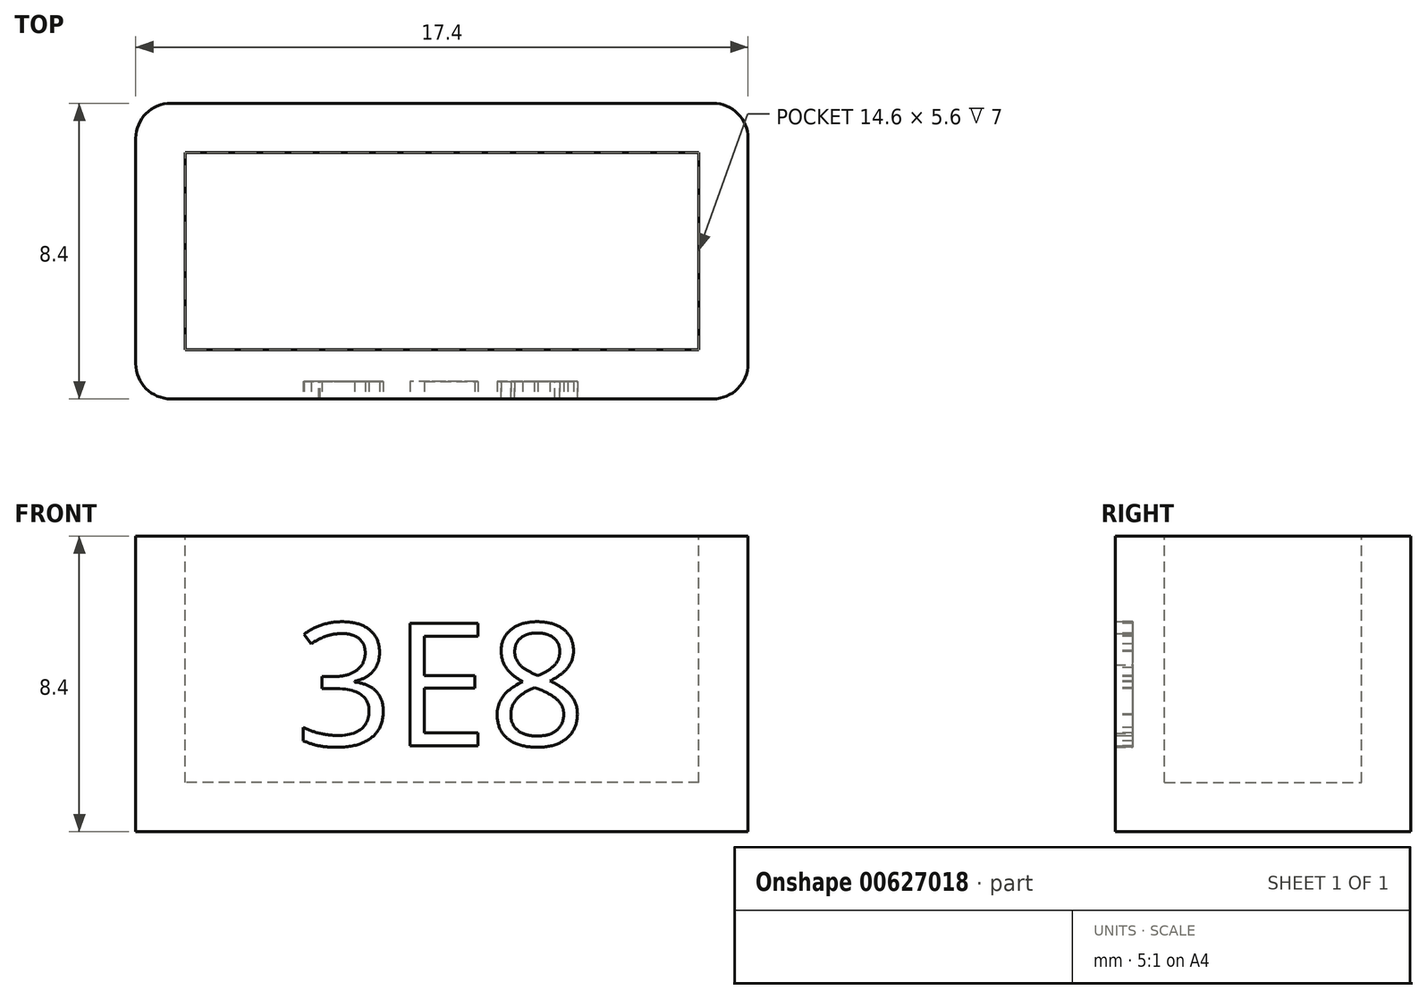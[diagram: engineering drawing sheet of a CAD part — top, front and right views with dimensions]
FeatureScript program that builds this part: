
annotation { "Feature Type Name" : "Feature", "Feature Type Description" : "" }
export const myFeature = defineFeature(function(context is Context, id is Id, definition is map)
    precondition{}
    {
        {
            assignVariable(context, id + "F0", {"name" : "h", "anyValue" : 7});
        }
        {
            assignVariable(context, id + "F1", {"name" : "wallthick", "anyValue" : 1.4});
        }
        {
            var Q0;
            Q0=qCreatedBy(makeId("Top.planeOp"),FACE);
            var sketch = newSketch(context, id + "F2", { "sketchPlane" : qUnion([Q0])});
            skLineSegment(sketch, "E0.bottom", {"start": v(8.7, -4.2) * mm, "end": v(-8.7, -4.2) * mm});
            skLineSegment(sketch, "E0.top", {"start": v(8.7, 4.2) * mm, "end": v(-8.7, 4.2) * mm});
            skLineSegment(sketch, "E0.left", {"start": v(8.7, -4.2) * mm, "end": v(8.7, 4.2) * mm});
            skLineSegment(sketch, "E0.right", {"start": v(-8.7, -4.2) * mm, "end": v(-8.7, 4.2) * mm});
            skPoint(sketch, "E0.middle", {"position": v(0, 0) * mm});
            skSolve(sketch);
        }
        {
            var Q0;
            Q0 = qSketchRegion(id + "F2", true);
            extrude(context, id + "F3", {"entities" : qUnion([Q0]), "depth" : (getVariable(context, 'h') + getVariable(context, 'wallthick')) * mm, "offsetDistance" : 25 * mm});
        }
        {
            var Q0;
            Q0=makeQuery(id+"F3.opExtrude","CAP_FACE",FACE,{"disambiguationData":[OSD([sQuery(id+"F2.wireOp",EDGE,"E0.bottom"),sQuery(id+"F2.wireOp",EDGE,"E0.top"),sQuery(id+"F2.wireOp",EDGE,"E0.left"),sQuery(id+"F2.wireOp",EDGE,"E0.right")])],"isStart":false});
            var sketch = newSketch(context, id + "F4", { "sketchPlane" : qUnion([Q0])});
            skLineSegment(sketch, "E1.bottom", {"start": v(7.3, -2.8) * mm, "end": v(-7.3, -2.8) * mm});
            skLineSegment(sketch, "E1.top", {"start": v(7.3, 2.8) * mm, "end": v(-7.3, 2.8) * mm});
            skLineSegment(sketch, "E1.left", {"start": v(7.3, -2.8) * mm, "end": v(7.3, 2.8) * mm});
            skLineSegment(sketch, "E1.right", {"start": v(-7.3, -2.8) * mm, "end": v(-7.3, 2.8) * mm});
            skPoint(sketch, "E1.middle", {"position": v(0, 0) * mm});
            skSolve(sketch);
        }
        {
            var Q0;
            Q0 = qSketchRegion(id + "F4", true);
            extrude(context, id + "F5", {"entities" : qUnion([Q0]), "operationType" : NewBodyOperationType.REMOVE, "oppositeDirection" : true, "depth" : (getVariable(context, 'h')) * mm, "offsetDistance" : 25 * mm});
        }
        {
            var Q0;
            Q0=makeQuery(id+"F3.opExtrude","SWEPT_FACE",FACE,{"disambiguationData":[OSD([sQuery(id+"F2.wireOp",EDGE,"E0.bottom")])]});
            var sketch = newSketch(context, id + "F6", { "sketchPlane" : qUnion([Q0])});
            skText(sketch, "E2", { "text": "3E8", "fontName": "OpenSans-Regular.ttf"});
            skLineSegment(sketch, "E3", {"start": v(8.7, 8.4) * mm, "end": v(-8.7, 0) * mm, "construction": true});
            skPoint(sketch, "E4", {"position": v(0, 4.2) * mm});
            skPoint(sketch, "E4.positionSnap0", {"position": v(0, 4.2) * mm});
            skPoint(sketch, "E4.positionSnap1", {"position": v(0, 4.2) * mm});
            const initialGuessF6  = {"E2": [-0.00416, 0.00245, 1, 0, 0.0035]};
            skSetInitialGuess(sketch, initialGuessF6);
            skSolve(sketch);
        }
        {
            var Q0;
            Q0 = qSketchRegion(id + "F6", true);
            extrude(context, id + "F7", {"entities" : qUnion([Q0]), "operationType" : NewBodyOperationType.REMOVE, "oppositeDirection" : true, "depth" : .5 * mm, "offsetDistance" : 25 * mm});
        }
        {
            var Q0;
            Q0=makeQuery(id+"F3.opExtrude","SWEPT_EDGE",EDGE,{"disambiguationData":[OSD([sQuery(id+"F2.wireOp",EDGE,"E0.bottom"),sQuery(id+"F2.wireOp",EDGE,"E0.left")])]});
            var Q1;
            Q1=makeQuery(id+"F3.opExtrude","SWEPT_EDGE",EDGE,{"disambiguationData":[OSD([sQuery(id+"F2.wireOp",EDGE,"E0.top"),sQuery(id+"F2.wireOp",EDGE,"E0.left")])]});
            var Q2;
            Q2=makeQuery(id+"F3.opExtrude","SWEPT_EDGE",EDGE,{"disambiguationData":[OSD([sQuery(id+"F2.wireOp",EDGE,"E0.top"),sQuery(id+"F2.wireOp",EDGE,"E0.right")])]});
            var Q3;
            Q3=makeQuery(id+"F3.opExtrude","SWEPT_EDGE",EDGE,{"disambiguationData":[OSD([sQuery(id+"F2.wireOp",EDGE,"E0.bottom"),sQuery(id+"F2.wireOp",EDGE,"E0.right")])]});
            fillet(context, id + "F8", {"entities" : qUnion([Q0, Q1, Q2, Q3]), "radius" : 1 * mm, "tangentPropagation" : true, "allowEdgeOverflow" : false});
        }
    });
